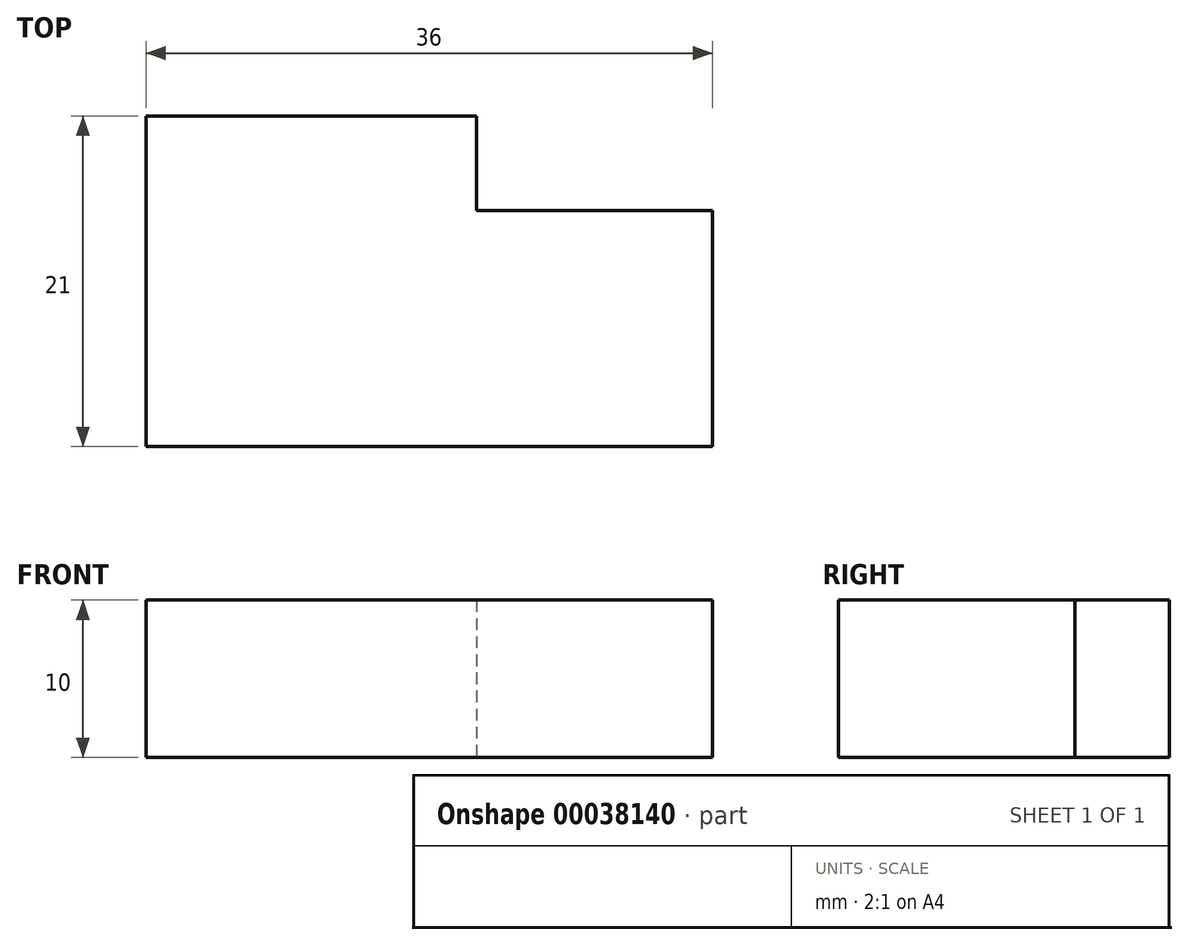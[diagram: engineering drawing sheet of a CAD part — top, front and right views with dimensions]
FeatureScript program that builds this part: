
annotation { "Feature Type Name" : "Feature", "Feature Type Description" : "" }
export const myFeature = defineFeature(function(context is Context, id is Id, definition is map)
    precondition{}
    {
        {
            var Q0;
            Q0=qCreatedBy(makeId("Top.planeOp"),FACE);
            var sketch = newSketch(context, id + "F0", { "sketchPlane" : qUnion([Q0])});
            skLineSegment(sketch, "E0.bottom", {"start": v(0, -1.79) * mm, "end": v(-21, -1.79) * mm});
            skLineSegment(sketch, "E0.top", {"start": v(0, 19.21) * mm, "end": v(-21, 19.21) * mm});
            skLineSegment(sketch, "E0.left", {"start": v(0, -1.79) * mm, "end": v(0, 19.21) * mm});
            skLineSegment(sketch, "E0.right", {"start": v(-21, -1.79) * mm, "end": v(-21, 19.21) * mm});
            skLineSegment(sketch, "E1.bottom", {"start": v(-21, 19.21) * mm, "end": v(-7, 19.21) * mm});
            skLineSegment(sketch, "E1.top", {"start": v(-21, 33.21) * mm, "end": v(-7, 33.21) * mm});
            skLineSegment(sketch, "E1.left", {"start": v(-21, 19.21) * mm, "end": v(-21, 33.21) * mm});
            skLineSegment(sketch, "E1.right", {"start": v(-7, 19.21) * mm, "end": v(-7, 33.21) * mm});
            skLineSegment(sketch, "E2.bottom", {"start": v(0, -1.79) * mm, "end": v(15, -1.79) * mm});
            skLineSegment(sketch, "E2.top", {"start": v(0, 13.21) * mm, "end": v(15, 13.21) * mm});
            skLineSegment(sketch, "E2.left", {"start": v(0, -1.79) * mm, "end": v(0, 13.21) * mm});
            skLineSegment(sketch, "E2.right", {"start": v(15, -1.79) * mm, "end": v(15, 13.21) * mm});
            skSolve(sketch);
        }
        {
            var Q0;
            Q0=makeQuery(id+"F0.imprint","IMPRINT",FACE,{"disambiguationData":[TD([[makeQuery(id+"F0.imprint","IMPRINT",EDGE,{"derivedFrom":sQuery(id+"F0.wireOp",EDGE,"E0.bottom")}),-1.0]])]});
            var Q1;
            Q1=makeQuery(id+"F0.imprint","IMPRINT",FACE,{"disambiguationData":[TD([[makeQuery(id+"F0.imprint","IMPRINT",EDGE,{"derivedFrom":sQuery(id+"F0.wireOp",EDGE,"E1.bottom")}),1.0]])]});
            var Q2;
            Q2=makeQuery(id+"F0.imprint","IMPRINT",FACE,{"disambiguationData":[TD([[makeQuery(id+"F0.imprint","IMPRINT",EDGE,{"derivedFrom":sQuery(id+"F0.wireOp",EDGE,"E2.bottom")}),1.0]])]});
            extrude(context, id + "F1", {"entities" : qUnion([Q0, Q1, Q2]), "depth" : 10 * mm});
        }
    });
